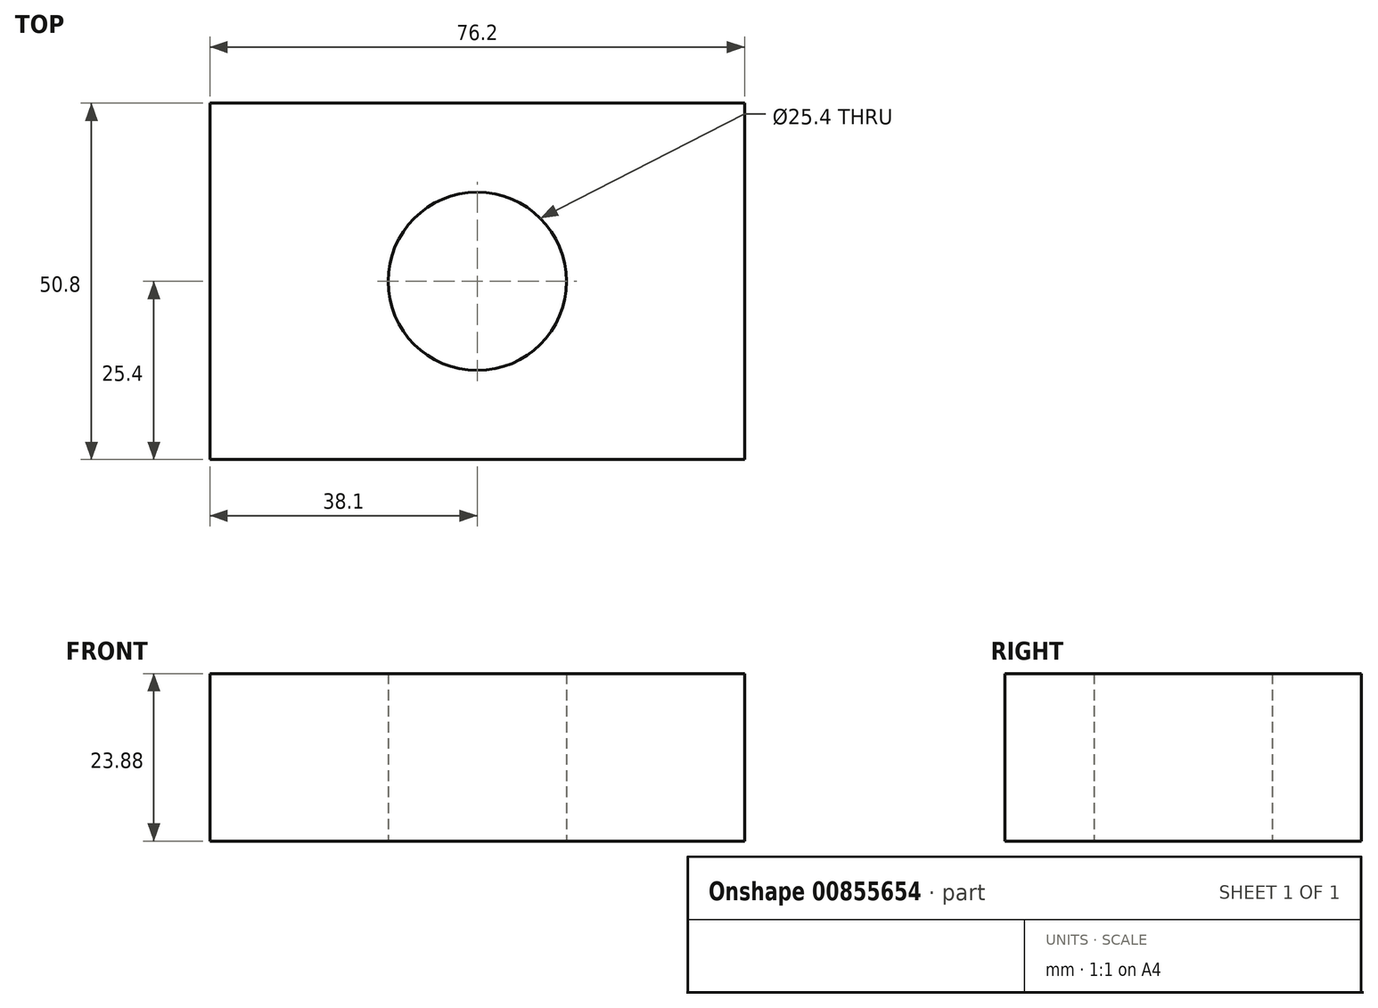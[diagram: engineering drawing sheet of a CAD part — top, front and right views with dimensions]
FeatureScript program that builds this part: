
annotation { "Feature Type Name" : "Feature", "Feature Type Description" : "" }
export const myFeature = defineFeature(function(context is Context, id is Id, definition is map)
    precondition{}
    {
        {
            var Q0;
            Q0=qCreatedBy(makeId("Top.planeOp"),FACE);
            var sketch = newSketch(context, id + "F0", { "sketchPlane" : qUnion([Q0])});
            skLineSegment(sketch, "E0.bottom", {"start": v(38.1, 25.4) * mm, "end": v(-38.1, 25.4) * mm});
            skLineSegment(sketch, "E0.top", {"start": v(38.1, -25.4) * mm, "end": v(-38.1, -25.4) * mm});
            skLineSegment(sketch, "E0.left", {"start": v(38.1, 25.4) * mm, "end": v(38.1, -25.4) * mm});
            skLineSegment(sketch, "E0.right", {"start": v(-38.1, 25.4) * mm, "end": v(-38.1, -25.4) * mm});
            skPoint(sketch, "E0.middle", {"position": v(0, 0) * mm});
            skCircle(sketch, "E1", {"center": v(0, 0) * mm, "radius": 12.7 * mm});
            skSolve(sketch);
        }
        {
            var Q0;
            Q0=makeQuery(id+"F0.imprint","IMPRINT",FACE,{"disambiguationData":[TD([[makeQuery(id+"F0.imprint","IMPRINT",EDGE,{"derivedFrom":sQuery(id+"F0.wireOp",EDGE,"E0.bottom")}),1.0]])]});
            extrude(context, id + "F1", {"entities" : qUnion([Q0]), "depth" : 23.88 * mm, "offsetDistance" : 25.4 * mm});
        }
    });
